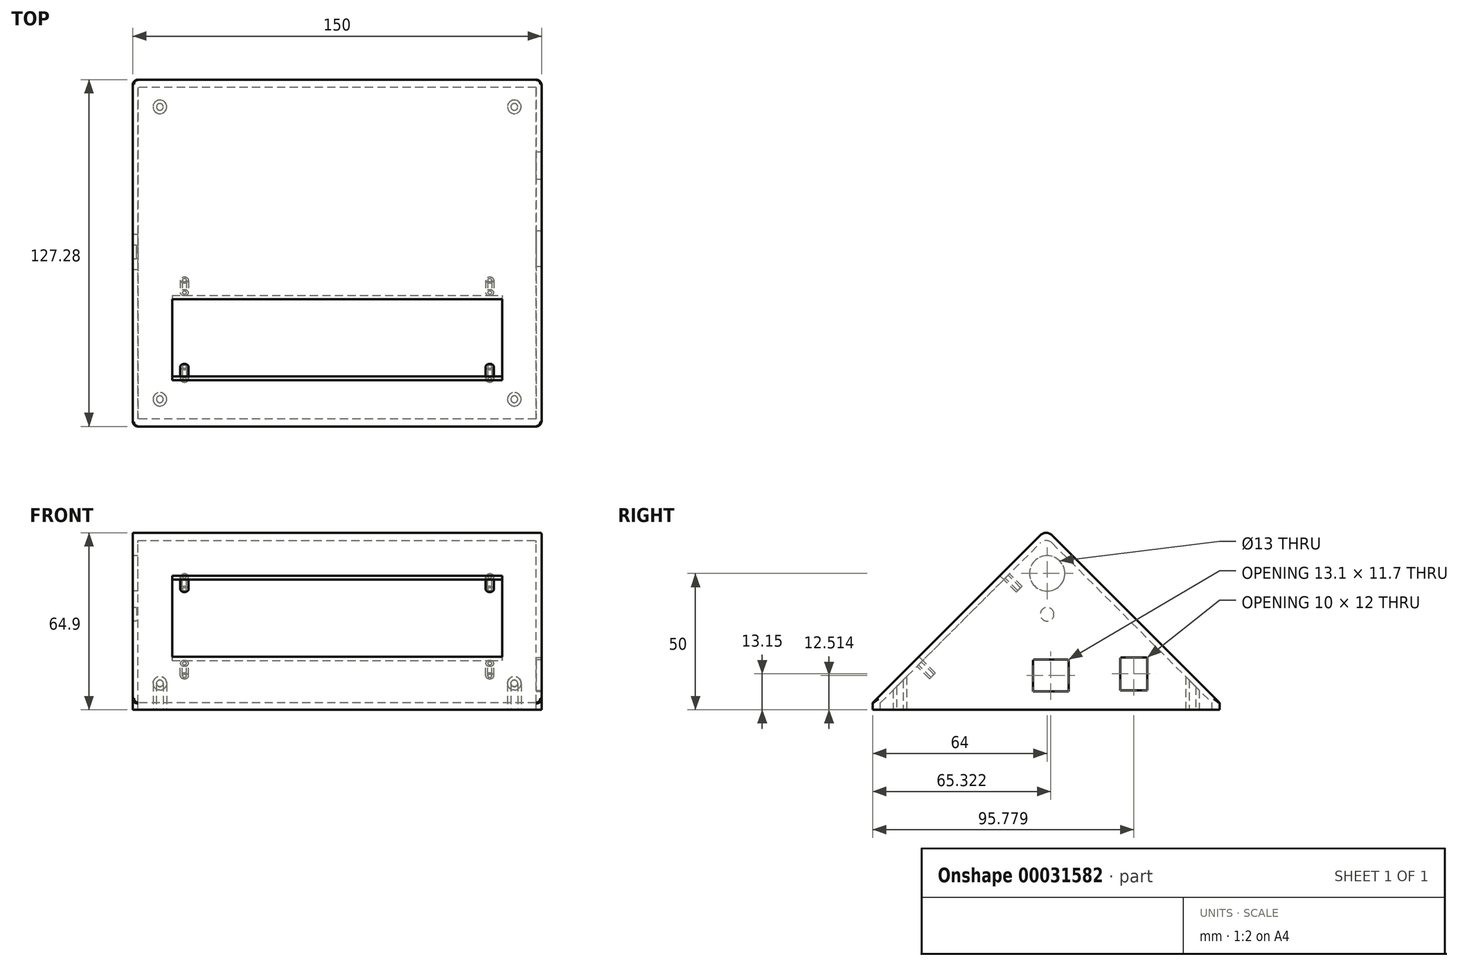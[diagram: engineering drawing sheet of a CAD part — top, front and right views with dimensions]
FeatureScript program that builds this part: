
annotation { "Feature Type Name" : "Feature", "Feature Type Description" : "" }
export const myFeature = defineFeature(function(context is Context, id is Id, definition is map)
    precondition{}
    {
        {
            var Q0;
            Q0=qCreatedBy(makeId("Right.planeOp"),FACE);
            var sketch = newSketch(context, id + "F0", { "sketchPlane" : qUnion([Q0])});
            skLineSegment(sketch, "E0", {"start": v(0, 0) * mm, "end": v(63.64, 63.64) * mm});
            skLineSegment(sketch, "E1", {"start": v(63.64, 63.64) * mm, "end": v(127.28, 0) * mm});
            skLineSegment(sketch, "E2", {"start": v(127.28, 0) * mm, "end": v(0, 0) * mm});
            skSolve(sketch);
        }
        {
            var Q0;
            Q0=qSketchRegion(id+"F0",true);
            extrude(context, id + "F1", {"entities" : qUnion([Q0]), "depth" : 150 * mm});
        }
        {
            var Q0;
            Q0=makeQuery(id+"F1.opExtrude","SWEPT_FACE",FACE,{"disambiguationData":[OSD([sQuery(id+"F0.wireOp",EDGE,"E2")])]});
            shell(context, id + "F2", {"entities" : qUnion([Q0]), "thickness" : 2 * mm});
        }
        {
            var Q0;
            Q0=makeQuery(id+"F1.opExtrude","SWEPT_FACE",FACE,{"disambiguationData":[OSD([sQuery(id+"F0.wireOp",EDGE,"E0")])]});
            cPlane(context, id + "F3", {"entities" : qUnion([Q0]), "cplaneType" : CPlaneType.OFFSET, "offset" : 0 * mm, "width" : 150 * mm, "height" : 150 * mm});
        }
        {
            var Q0;
            Q0=qCreatedBy(id+"F3.planeOp",FACE);
            var sketch = newSketch(context, id + "F4", { "sketchPlane" : qUnion([Q0])});
            skLineSegment(sketch, "E3.bottom", {"start": v(14.5, 66) * mm, "end": v(135.5, 66) * mm});
            skLineSegment(sketch, "E3.top", {"start": v(14.5, 24) * mm, "end": v(135.5, 24) * mm});
            skLineSegment(sketch, "E3.left", {"start": v(14.5, 66) * mm, "end": v(14.5, 24) * mm});
            skLineSegment(sketch, "E3.right", {"start": v(135.5, 66) * mm, "end": v(135.5, 24) * mm});
            skLineSegment(sketch, "E4", {"start": v(14.5, 45) * mm, "end": v(90.75, 45) * mm, "construction": true});
            skSolve(sketch);
        }
        {
            var Q0;
            Q0=qSketchRegion(id+"F4",true);
            extrude(context, id + "F5", {"entities" : qUnion([Q0]), "operationType" : NewBodyOperationType.REMOVE, "oppositeDirection" : true, "depth" : 3 * mm});
        }
        {
            var Q0;
            Q0=makeQuery(id+"F1.opExtrude","SWEPT_EDGE",EDGE,{"disambiguationData":[OSD([sQuery(id+"F0.wireOp",EDGE,"E0"),sQuery(id+"F0.wireOp",EDGE,"E1")])]});
            fillet(context, id + "F6", {"entities" : qUnion([Q0]), "radius" : 3 * mm, "tangentPropagation" : true, "allowEdgeOverflow" : false});
        }
        {
            var Q0;
            Q0=makeQuery(id+"F1.opExtrude","CAP_FACE",FACE,{"disambiguationData":[OSD([sQuery(id+"F0.wireOp",EDGE,"E0"),sQuery(id+"F0.wireOp",EDGE,"E1"),sQuery(id+"F0.wireOp",EDGE,"E2")])],"isStart":false});
            var sketch = newSketch(context, id + "F7", { "sketchPlane" : qUnion([Q0])});
            skCircle(sketch, "E5", {"center": v(70, 8) * mm, "radius": 6 * mm, "construction": true});
            skLineSegment(sketch, "E6.bottom", {"start": v(90.78, 4.65) * mm, "end": v(100.78, 4.65) * mm});
            skLineSegment(sketch, "E6.top", {"start": v(90.78, 16.65) * mm, "end": v(100.78, 16.65) * mm});
            skLineSegment(sketch, "E6.left", {"start": v(90.78, 4.65) * mm, "end": v(90.78, 16.65) * mm});
            skLineSegment(sketch, "E6.right", {"start": v(100.78, 4.65) * mm, "end": v(100.78, 16.65) * mm});
            skLineSegment(sketch, "E7.bottom", {"start": v(59.27, 15.36) * mm, "end": v(71.37, 15.36) * mm, "construction": true});
            skLineSegment(sketch, "E7.top", {"start": v(59.27, 4.66) * mm, "end": v(71.37, 4.66) * mm, "construction": true});
            skLineSegment(sketch, "E7.left", {"start": v(59.27, 15.36) * mm, "end": v(59.27, 4.66) * mm, "construction": true});
            skLineSegment(sketch, "E7.right", {"start": v(71.37, 15.36) * mm, "end": v(71.37, 4.66) * mm, "construction": true});
            skLineSegment(sketch, "E8", {"start": v(71.87, 15.86) * mm, "end": v(58.77, 15.86) * mm});
            skLineSegment(sketch, "E9", {"start": v(58.77, 15.86) * mm, "end": v(58.77, 4.16) * mm});
            skLineSegment(sketch, "E10", {"start": v(58.77, 4.16) * mm, "end": v(71.87, 4.16) * mm});
            skLineSegment(sketch, "E11", {"start": v(71.87, 15.86) * mm, "end": v(71.87, 4.16) * mm});
            skSolve(sketch);
        }
        {
            var Q0;
            Q0=makeQuery(id+"F1.opExtrude","SWEPT_FACE",FACE,{"disambiguationData":[OSD([sQuery(id+"F0.wireOp",EDGE,"E0")])]});
            var sketch = newSketch(context, id + "F8", { "sketchPlane" : qUnion([Q0])});
            skCircle(sketch, "E12", {"center": v(131, 22.5) * mm, "radius": 0.75 * mm});
            skCircle(sketch, "E13", {"center": v(131, 67.5) * mm, "radius": 0.75 * mm});
            skPoint(sketch, "E14.endSnap0", {"position": v(75, 66) * mm});
            skCircle(sketch, "E15", {"center": v(131, 67.5) * mm, "radius": 1.5 * mm});
            skCircle(sketch, "E16", {"center": v(131, 22.5) * mm, "radius": 1.5 * mm});
            skCircle(sketch, "E17", {"center": v(19, 67.5) * mm, "radius": 0.75 * mm});
            skCircle(sketch, "E18", {"center": v(19, 67.5) * mm, "radius": 1.5 * mm});
            skCircle(sketch, "E19", {"center": v(19, 22.5) * mm, "radius": 0.75 * mm});
            skCircle(sketch, "E20", {"center": v(19, 22.5) * mm, "radius": 1.5 * mm});
            skSolve(sketch);
        }
        {
            var Q0;
            Q0=qSketchRegion(id+"F8",true);
            extrude(context, id + "F9", {"entities" : qUnion([Q0]), "operationType" : NewBodyOperationType.ADD, "oppositeDirection" : true, "depth" : 8.5 * mm});
        }
        {
            var Q0;
            Q0=makeQuery(id+"F1.opExtrude","SWEPT_FACE",FACE,{"disambiguationData":[OSD([sQuery(id+"F0.wireOp",EDGE,"E2")])]});
            var sketch = newSketch(context, id + "F10", { "sketchPlane" : qUnion([Q0])});
            skCircle(sketch, "E21", {"center": v(10, -10) * mm, "radius": 1.5 * mm});
            skCircle(sketch, "E22", {"center": v(10, -10) * mm, "radius": 2.5 * mm});
            skSolve(sketch);
        }
        {
            var Q0;
            Q0=qSketchRegion(id+"F10",true);
            var Q1;
            Q1=makeQuery(id+"F1.opExtrude","SWEPT_FACE",FACE,{"disambiguationData":[OSD([sQuery(id+"F0.wireOp",EDGE,"E0")])]});
            extrude(context, id + "F11", {"entities" : qUnion([Q0]), "operationType" : NewBodyOperationType.ADD, "endBound" : BoundingType.UP_TO_SURFACE, "oppositeDirection" : true, "endBoundEntityFace" : qUnion([Q1]), "depth" : 25 * mm});
        }
        {
            var Q0;
            Q0=makeQuery(id+"F1.opExtrude","SWEPT_FACE",FACE,{"disambiguationData":[OSD([sQuery(id+"F0.wireOp",EDGE,"E2")])]});
            var sketch = newSketch(context, id + "F12", { "sketchPlane" : qUnion([Q0])});
            skCircle(sketch, "E23", {"center": v(10, -117.28) * mm, "radius": 2.5 * mm, "construction": true});
            skCircle(sketch, "E24", {"center": v(10, -117.28) * mm, "radius": 1.5 * mm, "construction": true});
            skCircle(sketch, "E25", {"center": v(140, -117.28) * mm, "radius": 1.5 * mm, "construction": true});
            skCircle(sketch, "E26", {"center": v(140, -117.28) * mm, "radius": 2.5 * mm, "construction": true});
            skCircle(sketch, "E27", {"center": v(10, -10) * mm, "radius": 1.25 * mm});
            skCircle(sketch, "E28", {"center": v(10, -10) * mm, "radius": 2.5 * mm});
            skCircle(sketch, "E29", {"center": v(140, -10) * mm, "radius": 1.25 * mm});
            skCircle(sketch, "E30", {"center": v(140, -10) * mm, "radius": 2.5 * mm});
            skSolve(sketch);
        }
        {
            var Q0;
            Q0=qSketchRegion(id+"F12",true);
            var Q1;
            {var subQ1=sQuery(id+"F0.wireOp",EDGE,"E2");var subQ3=sQuery(id+"F0.wireOp",EDGE,"E0");var subQ13=makeQuery(id+"F1.opExtrude","SWEPT_FACE",FACE,{"disambiguationData":[OSD([subQ1])]});Q1=makeQuery(id+"F11.boolean.opBoolean","SPLIT",FACE,{"disambiguationData":[TD([subQ13])],"derivedFrom":makeQuery(id+"F9.boolean.opBoolean","SPLIT",FACE,{"disambiguationData":[TD([subQ13])],"derivedFrom":makeQuery(id+"F2.opShell","OFFSET_FACE",FACE,{"disambiguationData":[OSD([subQ3])]})})});}
            extrude(context, id + "F13", {"entities" : qUnion([Q0]), "operationType" : NewBodyOperationType.ADD, "endBound" : BoundingType.UP_TO_SURFACE, "oppositeDirection" : true, "endBoundEntityFace" : qUnion([Q1]), "depth" : 25 * mm});
        }
        {
            var Q0;
            Q0=makeQuery(id+"F1.opExtrude","SWEPT_FACE",FACE,{"disambiguationData":[OSD([sQuery(id+"F0.wireOp",EDGE,"E2")])]});
            var sketch = newSketch(context, id + "F14", { "sketchPlane" : qUnion([Q0])});
            skLineSegment(sketch, "E31.bottom", {"start": v(0, 0) * mm, "end": v(150, 0) * mm});
            skLineSegment(sketch, "E31.top", {"start": v(0, -127.28) * mm, "end": v(150, -127.28) * mm});
            skLineSegment(sketch, "E31.left", {"start": v(0, 0) * mm, "end": v(0, -127.28) * mm});
            skLineSegment(sketch, "E31.right", {"start": v(150, 0) * mm, "end": v(150, -127.28) * mm});
            skLineSegment(sketch, "E32.bottom", {"start": v(148, -124.45) * mm, "end": v(2, -124.45) * mm});
            skLineSegment(sketch, "E32.top", {"start": v(148, -2.83) * mm, "end": v(2, -2.83) * mm});
            skLineSegment(sketch, "E32.left", {"start": v(148, -124.45) * mm, "end": v(148, -2.83) * mm});
            skLineSegment(sketch, "E32.right", {"start": v(2, -124.45) * mm, "end": v(2, -2.83) * mm});
            skSolve(sketch);
        }
        {
            var Q0;
            Q0=qSketchRegion(id+"F14",true);
            extrude(context, id + "F15", {"entities" : qUnion([Q0]), "operationType" : NewBodyOperationType.ADD, "depth" : 2.5 * mm});
        }
        {
            var Q0;
            Q0=qCreatedBy(makeId("Top.planeOp"),FACE);
            var sketch = newSketch(context, id + "F16", { "sketchPlane" : qUnion([Q0])});
            skCircle(sketch, "E33", {"center": v(10, 117.28) * mm, "radius": 1.25 * mm});
            skCircle(sketch, "E34.0", {"center": v(10, 10) * mm, "radius": 2.5 * mm, "construction": true});
            skCircle(sketch, "E35", {"center": v(10, 117.28) * mm, "radius": 2.5 * mm});
            skCircle(sketch, "E36", {"center": v(140, 117.28) * mm, "radius": 1.25 * mm});
            skCircle(sketch, "E37", {"center": v(140, 117.28) * mm, "radius": 2.5 * mm});
            skCircle(sketch, "E38.0", {"center": v(140, 10) * mm, "radius": 1.25 * mm});
            skSolve(sketch);
        }
        {
            var Q0;
            Q0=makeQuery(id+"F16.imprint","IMPRINT",FACE,{"disambiguationData":[TD([[makeQuery(id+"F16.imprint","IMPRINT",EDGE,{"derivedFrom":sQuery(id+"F16.wireOp",EDGE,"E36")}),-1.0]])]});
            var Q1;
            Q1=makeQuery(id+"F16.imprint","IMPRINT",FACE,{"disambiguationData":[TD([[makeQuery(id+"F16.imprint","IMPRINT",EDGE,{"derivedFrom":sQuery(id+"F16.wireOp",EDGE,"E33")}),-1.0]])]});
            var Q2;
            Q2=makeQuery(id+"F2.opShell","OFFSET_FACE",FACE,{"disambiguationData":[OSD([sQuery(id+"F0.wireOp",EDGE,"E1")])]});
            extrude(context, id + "F17", {"entities" : qUnion([Q0, Q1]), "operationType" : NewBodyOperationType.ADD, "endBound" : BoundingType.UP_TO_SURFACE, "endBoundEntityFace" : qUnion([Q2]), "depth" : 25 * mm});
        }
        {
            var Q0;
            Q0=makeQuery(id+"F15.opExtrude","SWEPT_EDGE",EDGE,{"disambiguationData":[OSD([sQuery(id+"F14.wireOp",EDGE,"E31.top"),sQuery(id+"F14.wireOp",EDGE,"E31.right")])]});
            var Q1;
            Q1=makeQuery(id+"F15.opExtrude","SWEPT_EDGE",EDGE,{"disambiguationData":[OSD([sQuery(id+"F14.wireOp",EDGE,"E31.bottom"),sQuery(id+"F14.wireOp",EDGE,"E31.right")])]});
            var Q2;
            Q2=makeQuery(id+"F15.opExtrude","SWEPT_EDGE",EDGE,{"disambiguationData":[OSD([sQuery(id+"F14.wireOp",EDGE,"E31.bottom"),sQuery(id+"F14.wireOp",EDGE,"E31.left")])]});
            var Q3;
            Q3=makeQuery(id+"F15.opExtrude","SWEPT_EDGE",EDGE,{"disambiguationData":[OSD([sQuery(id+"F14.wireOp",EDGE,"E31.top"),sQuery(id+"F14.wireOp",EDGE,"E31.left")])]});
            fillet(context, id + "F18", {"entities" : qUnion([Q0, Q1, Q2, Q3]), "radius" : 2 * mm, "tangentPropagation" : true, "allowEdgeOverflow" : false});
        }
        {
            var Q0;
            Q0=makeQuery(id+"F1.opExtrude","CAP_EDGE",EDGE,{"disambiguationData":[OSD([sQuery(id+"F0.wireOp",EDGE,"E0")])],"isStart":true});
            fillet(context, id + "F19", {"entities" : qUnion([Q0]), "radius" : 0.5 * mm, "tangentPropagation" : true, "allowEdgeOverflow" : false});
        }
        {
            var Q0;
            Q0=qSketchRegion(id+"F7",true);
            extrude(context, id + "F20", {"entities" : qUnion([Q0]), "operationType" : NewBodyOperationType.REMOVE, "oppositeDirection" : true, "depth" : 3 * mm});
        }
        {
            var Q0;
            Q0=makeQuery(id+"F20.boolean.opBoolean","COPY",EDGE,{"derivedFrom":makeQuery(id+"F20.opExtrude","SWEPT_EDGE",EDGE,{"disambiguationData":[OSD([sQuery(id+"F7.wireOp",EDGE,"E6.top"),sQuery(id+"F7.wireOp",EDGE,"E6.left")])]})});
            var Q1;
            Q1=makeQuery(id+"F20.boolean.opBoolean","COPY",EDGE,{"derivedFrom":makeQuery(id+"F20.opExtrude","SWEPT_EDGE",EDGE,{"disambiguationData":[OSD([sQuery(id+"F7.wireOp",EDGE,"E6.top"),sQuery(id+"F7.wireOp",EDGE,"E6.right")])]})});
            fillet(context, id + "F21", {"entities" : qUnion([Q0, Q1]), "radius" : 0.5 * mm, "tangentPropagation" : true, "allowEdgeOverflow" : false});
        }
        {
            var Q0;
            Q0=makeQuery(id+"F20.boolean.opBoolean","COPY",EDGE,{"derivedFrom":makeQuery(id+"F20.opExtrude","SWEPT_EDGE",EDGE,{"disambiguationData":[OSD([sQuery(id+"F7.wireOp",EDGE,"E8"),sQuery(id+"F7.wireOp",EDGE,"E11")])]})});
            var Q1;
            Q1=makeQuery(id+"F20.boolean.opBoolean","COPY",EDGE,{"derivedFrom":makeQuery(id+"F20.opExtrude","SWEPT_EDGE",EDGE,{"disambiguationData":[OSD([sQuery(id+"F7.wireOp",EDGE,"E8"),sQuery(id+"F7.wireOp",EDGE,"E9")])]})});
            fillet(context, id + "F22", {"entities" : qUnion([Q0, Q1]), "radius" : .5 * mm, "tangentPropagation" : true, "allowEdgeOverflow" : false});
        }
        {
            var Q0;
            Q0=makeQuery(id+"F15.boolean.opBoolean","MERGE",FACE,{"derivedFrom":[makeQuery(id+"F1.opExtrude","CAP_FACE",FACE,{"disambiguationData":[OSD([sQuery(id+"F0.wireOp",EDGE,"E0"),sQuery(id+"F0.wireOp",EDGE,"E1"),sQuery(id+"F0.wireOp",EDGE,"E2")])],"isStart":true}),makeQuery(id+"F15.opExtrude","SWEPT_FACE",FACE,{"disambiguationData":[OSD([sQuery(id+"F14.wireOp",EDGE,"E31.left")])]})]});
            var sketch = newSketch(context, id + "F23", { "sketchPlane" : qUnion([Q0])});
            skCircle(sketch, "E39", {"center": v(-64, 47.5) * mm, "radius": 6.5 * mm});
            skSolve(sketch);
        }
        {
            var Q0;
            Q0=makeQuery(id+"F23.imprint","IMPRINT",FACE,{"disambiguationData":[TD([[makeQuery(id+"F23.imprint","IMPRINT",EDGE,{"derivedFrom":sQuery(id+"F23.wireOp",EDGE,"E39")}),1.0]])]});
            var Q1;
            Q1=sQuery(id+"F23.wireOp",EDGE,"E39");
            extrude(context, id + "F24", {"entities" : qUnion([Q0]), "operationType" : NewBodyOperationType.REMOVE, "surfaceEntities" : qUnion([Q1]), "oppositeDirection" : true, "depth" : 2.5 * mm});
        }
        {
            var Q0;
            Q0=makeQuery(id+"F13.opExtrude","CAP_FACE",FACE,{"disambiguationData":[OSD([sQuery(id+"F12.wireOp",EDGE,"E29"),sQuery(id+"F12.wireOp",EDGE,"E30")])],"isStart":true});
            var sketch = newSketch(context, id + "F25", { "sketchPlane" : qUnion([Q0])});
            skCircle(sketch, "E40", {"center": v(140, -10) * mm, "radius": 1.25 * mm});
            skCircle(sketch, "E41.0", {"center": v(10, -10) * mm, "radius": 1.25 * mm});
            skCircle(sketch, "E42.0", {"center": v(10, -10) * mm, "radius": 2.5 * mm});
            skCircle(sketch, "E43.0", {"center": v(140, -10) * mm, "radius": 2.5 * mm});
            skCircle(sketch, "E44.0", {"center": v(10, -117.28) * mm, "radius": 1.25 * mm});
            skCircle(sketch, "E45.0", {"center": v(10, -117.28) * mm, "radius": 2.5 * mm});
            skCircle(sketch, "E46.0", {"center": v(140, -117.28) * mm, "radius": 1.25 * mm});
            skCircle(sketch, "E47.0", {"center": v(140, -117.28) * mm, "radius": 2.5 * mm});
            skSolve(sketch);
        }
        {
            var Q0;
            Q0=qSketchRegion(id+"F25",true);
            extrude(context, id + "F26", {"entities" : qUnion([Q0]), "operationType" : NewBodyOperationType.ADD, "depth" : 2.5 * mm});
        }
        {
            var Q0;
            Q0=makeQuery(id+"F15.boolean.opBoolean","MERGE",FACE,{"derivedFrom":[makeQuery(id+"F1.opExtrude","CAP_FACE",FACE,{"disambiguationData":[OSD([sQuery(id+"F0.wireOp",EDGE,"E0"),sQuery(id+"F0.wireOp",EDGE,"E1"),sQuery(id+"F0.wireOp",EDGE,"E2")])],"isStart":true}),makeQuery(id+"F15.opExtrude","SWEPT_FACE",FACE,{"disambiguationData":[OSD([sQuery(id+"F14.wireOp",EDGE,"E31.left")])]})]});
            var sketch = newSketch(context, id + "F27", { "sketchPlane" : qUnion([Q0])});
            skCircle(sketch, "E48", {"center": v(-64, 32.5) * mm, "radius": 2.5 * mm});
            skCircle(sketch, "E49.0", {"center": v(-64, 47.5) * mm, "radius": 6.5 * mm, "construction": true});
            skCircle(sketch, "E50", {"center": v(-64, 47.5) * mm, "radius": 7 * mm, "construction": true});
            skSolve(sketch);
        }
        {
            var Q0;
            Q0=makeQuery(id+"F27.imprint","IMPRINT",FACE,{"disambiguationData":[TD([[makeQuery(id+"F27.imprint","IMPRINT",EDGE,{"derivedFrom":sQuery(id+"F27.wireOp",EDGE,"E48")}),1.0]])]});
            var Q1;
            Q1=sQuery(id+"F27.wireOp",EDGE,"E50");
            var Q2;
            Q2=sQuery(id+"F27.wireOp",EDGE,"E49.0");
            extrude(context, id + "F28", {"entities" : qUnion([Q0]), "operationType" : NewBodyOperationType.REMOVE, "surfaceEntities" : qUnion([Q1, Q2]), "oppositeDirection" : true, "depth" : 1.5 * mm});
        }
        {
            var Q0;
            Q0=makeQuery(id+"F2.opShell","OFFSET_EDGE",EDGE,{"disambiguationData":[OSD([sQuery(id+"F0.wireOp",EDGE,"E0"),sQuery(id+"F0.wireOp",EDGE,"E1")])]});
            fillet(context, id + "F29", {"entities" : qUnion([Q0]), "radius" : 3 * mm, "tangentPropagation" : true, "allowEdgeOverflow" : false});
        }
    });
